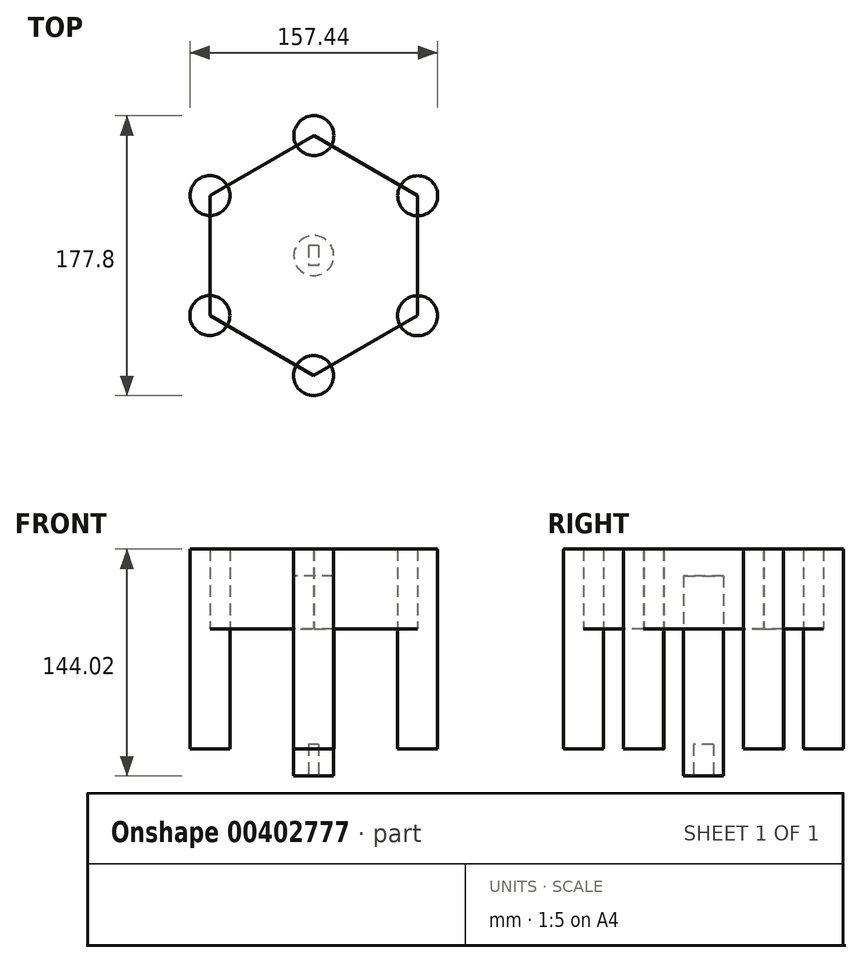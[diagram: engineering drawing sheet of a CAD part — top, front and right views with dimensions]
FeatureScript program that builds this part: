
annotation { "Feature Type Name" : "Feature", "Feature Type Description" : "" }
export const myFeature = defineFeature(function(context is Context, id is Id, definition is map)
    precondition{}
    {
        {
            var Q0;
            Q0=qCreatedBy(makeId("Top.planeOp"),FACE);
            var sketch = newSketch(context, id + "F0", { "sketchPlane" : qUnion([Q0])});
            skCircle(sketch, "E0", {"center": v(0, 0) * mm, "radius": 12.7 * mm});
            skSolve(sketch);
        }
        {
            var Q0;
            Q0 = qSketchRegion(id + "F0", true);
            extrude(context, id + "F1", {"entities" : qUnion([Q0]), "depth" : 127 * mm});
        }
        {
            var Q0;
            Q0=qCreatedBy(makeId("Top.planeOp"),FACE);
            var sketch = newSketch(context, id + "F2", { "sketchPlane" : qUnion([Q0])});
            skLineSegment(sketch, "E1.bottom", {"start": v(3.18, 6.35) * mm, "end": v(-3.18, 6.35) * mm});
            skLineSegment(sketch, "E1.top", {"start": v(3.18, -6.35) * mm, "end": v(-3.18, -6.35) * mm});
            skLineSegment(sketch, "E1.left", {"start": v(3.18, 6.35) * mm, "end": v(3.18, -6.35) * mm});
            skLineSegment(sketch, "E1.right", {"start": v(-3.18, 6.35) * mm, "end": v(-3.18, -6.35) * mm});
            skPoint(sketch, "E1.middle", {"position": v(0, 0) * mm});
            skSolve(sketch);
        }
        {
            var Q0;
            Q0 = qSketchRegion(id + "F2", true);
            extrude(context, id + "F3", {"entities" : qUnion([Q0]), "operationType" : NewBodyOperationType.REMOVE, "depth" : 20.07 * mm});
        }
        {
            var Q0;
            Q0=qCreatedBy(makeId("Top.planeOp"),FACE);
            cPlane(context, id + "F4", {"entities" : qUnion([Q0]), "cplaneType" : CPlaneType.OFFSET, "offset" : 93.22 * mm, "width" : 152.4 * mm, "height" : 152.4 * mm});
        }
        {
            var Q0;
            Q0=qCreatedBy(id+"F4.planeOp",FACE);
            var sketch = newSketch(context, id + "F5", { "sketchPlane" : qUnion([Q0])});
            skCircle(sketch, "E2.cCircle", {"center": v(0, 0) * mm, "radius": 76.2 * mm, "construction": true});
            skLineSegment(sketch, "E2.0", {"start": v(65.96, -38.16) * mm, "end": v(-0.07, -76.2) * mm});
            skLineSegment(sketch, "E2.1", {"start": v(-0.07, -76.2) * mm, "end": v(-66.02, -38.04) * mm});
            skLineSegment(sketch, "E2.2", {"start": v(-66.02, -38.04) * mm, "end": v(-65.96, 38.16) * mm});
            skLineSegment(sketch, "E2.3", {"start": v(-65.96, 38.16) * mm, "end": v(0.07, 76.2) * mm});
            skLineSegment(sketch, "E2.4", {"start": v(0.07, 76.2) * mm, "end": v(66.02, 38.04) * mm});
            skLineSegment(sketch, "E2.5", {"start": v(66.02, 38.04) * mm, "end": v(65.96, -38.16) * mm});
            skSolve(sketch);
        }
        {
            var Q0;
            Q0=qCreatedBy(id+"F4.planeOp",FACE);
            var sketch = newSketch(context, id + "F6", { "sketchPlane" : qUnion([Q0])});
            skCircle(sketch, "E3", {"center": v(65.96, -38.16) * mm, "radius": 12.7 * mm});
            skCircle(sketch, "E4", {"center": v(-0.07, -76.2) * mm, "radius": 12.7 * mm});
            skCircle(sketch, "E5", {"center": v(-66.02, -38.04) * mm, "radius": 12.7 * mm});
            skCircle(sketch, "E6", {"center": v(-65.96, 38.16) * mm, "radius": 12.7 * mm});
            skCircle(sketch, "E7", {"center": v(0.07, 76.2) * mm, "radius": 12.7 * mm});
            skCircle(sketch, "E8", {"center": v(66.02, 38.04) * mm, "radius": 12.7 * mm});
            skSolve(sketch);
        }
        {
            var Q0;
            Q0 = qSketchRegion(id + "F6", true);
            extrude(context, id + "F7", {"entities" : qUnion([Q0]), "operationType" : NewBodyOperationType.ADD, "depth" : 50.8 * mm, "hasSecondDirection" : true, "secondDirectionOppositeDirection" : true, "secondDirectionDepth" : 76.2 * mm});
        }
        {
            var Q0;
            Q0=makeQuery(id+"F5.imprint","IMPRINT",FACE,{"disambiguationData":[TD([[makeQuery(id+"F5.imprint","IMPRINT",EDGE,{"derivedFrom":sQuery(id+"F5.wireOp",EDGE,"E2.0")}),-1.0]])]});
            extrude(context, id + "F8", {"entities" : qUnion([Q0]), "depth" : 50.8 * mm});
        }
    });
